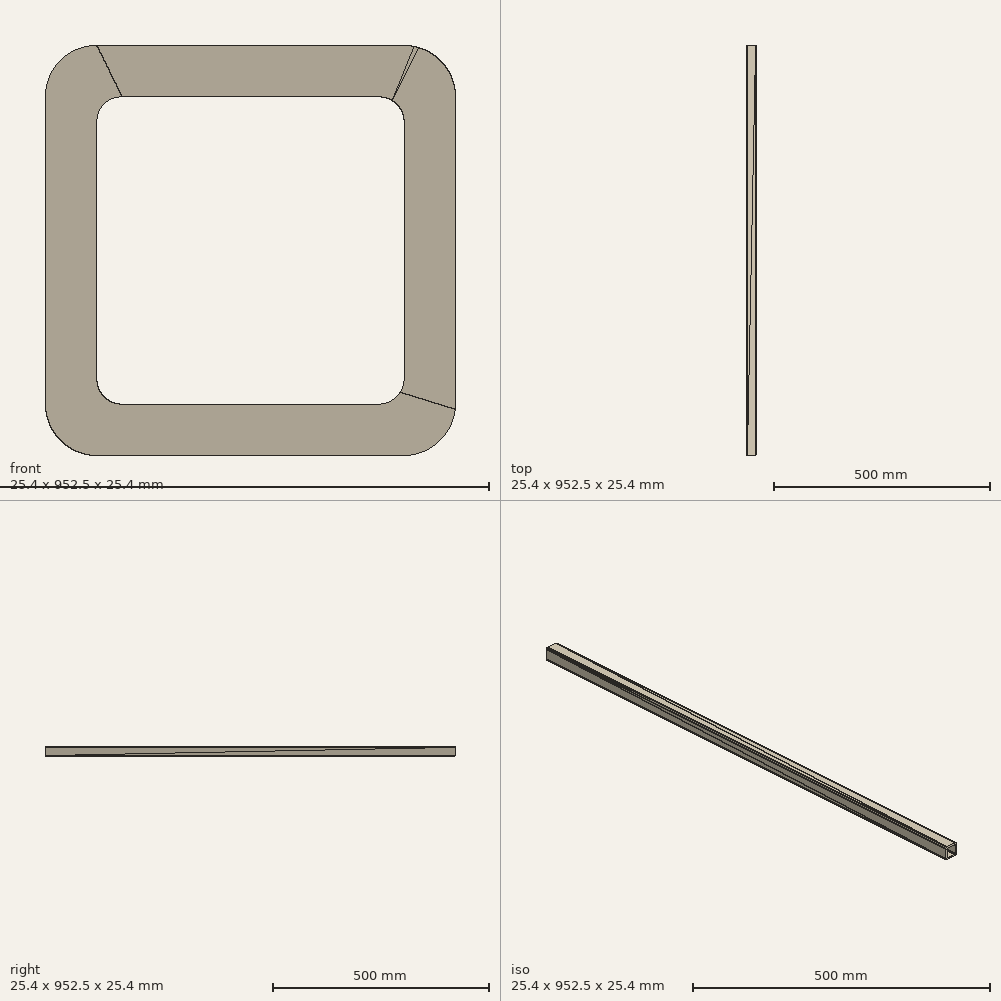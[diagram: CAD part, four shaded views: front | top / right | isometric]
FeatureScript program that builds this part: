
annotation { "Feature Type Name" : "Feature", "Feature Type Description" : "" }
export const myFeature = defineFeature(function(context is Context, id is Id, definition is map)
    precondition{}
    {
        {
            var Q0;
            Q0=qCreatedBy(makeId("Front.planeOp"),FACE);
            var sketch = newSketch(context, id + "F0", { "sketchPlane" : qUnion([Q0])});
            skLineSegment(sketch, "E0.bottom", {"start": v(3.18, 0) * mm, "end": v(22.23, 0) * mm});
            skLineSegment(sketch, "E0.top", {"start": v(3.17, 25.4) * mm, "end": v(22.23, 25.4) * mm});
            skLineSegment(sketch, "E0.left", {"start": v(0, 3.18) * mm, "end": v(0, 22.22) * mm});
            skLineSegment(sketch, "E0.right", {"start": v(25.4, 3.18) * mm, "end": v(25.4, 22.22) * mm});
            skPoint(sketch, "E1.visualSharp", {"position": v(0, 25.4) * mm});
            skArc(sketch, "E1.filletArc", {"start": v(3.17, 25.4) * mm, "mid": v(0.93, 24.47) * mm, "end": v(0, 22.22) * mm});
            skPoint(sketch, "E2.visualSharp", {"position": v(25.4, 25.4) * mm});
            skArc(sketch, "E2.filletArc", {"start": v(25.4, 22.22) * mm, "mid": v(24.47, 24.47) * mm, "end": v(22.23, 25.4) * mm});
            skPoint(sketch, "E3.visualSharp", {"position": v(25.4, 0) * mm});
            skArc(sketch, "E3.filletArc", {"start": v(22.23, 0) * mm, "mid": v(24.47, 0.93) * mm, "end": v(25.4, 3.18) * mm});
            skPoint(sketch, "E4.visualSharp", {"position": v(0, 0) * mm});
            skArc(sketch, "E4.filletArc", {"start": v(0, 3.18) * mm, "mid": v(0.93, 0.93) * mm, "end": v(3.18, 0) * mm});
            skSolve(sketch);
        }
        {
            var Q0;
            Q0 = qSketchRegion(id + "F0", true);
            extrude(context, id + "F1", {"entities" : qUnion([Q0]), "depth" : 952.5 * mm, "offsetDistance" : 25.4 * mm});
        }
        {
            var Q0;
            Q0=qCreatedBy(makeId("Front.planeOp"),FACE);
            var sketch = newSketch(context, id + "F2", { "sketchPlane" : qUnion([Q0])});
            skLineSegment(sketch, "E5.bottom", {"start": v(4.76, 3.18) * mm, "end": v(20.64, 3.18) * mm});
            skLineSegment(sketch, "E5.top", {"start": v(4.76, 22.23) * mm, "end": v(20.64, 22.23) * mm});
            skLineSegment(sketch, "E5.left", {"start": v(3.17, 4.76) * mm, "end": v(3.17, 20.64) * mm});
            skLineSegment(sketch, "E5.right", {"start": v(22.22, 4.76) * mm, "end": v(22.22, 20.64) * mm});
            skPoint(sketch, "E6.visualSharp", {"position": v(3.17, 22.23) * mm});
            skArc(sketch, "E6.filletArc", {"start": v(4.76, 22.23) * mm, "mid": v(3.64, 21.76) * mm, "end": v(3.17, 20.64) * mm});
            skPoint(sketch, "E7.visualSharp", {"position": v(22.22, 22.23) * mm});
            skArc(sketch, "E7.filletArc", {"start": v(22.22, 20.64) * mm, "mid": v(21.76, 21.76) * mm, "end": v(20.64, 22.23) * mm});
            skPoint(sketch, "E8.visualSharp", {"position": v(22.23, 3.18) * mm});
            skArc(sketch, "E8.filletArc", {"start": v(20.64, 3.18) * mm, "mid": v(21.76, 3.64) * mm, "end": v(22.22, 4.76) * mm});
            skPoint(sketch, "E9.visualSharp", {"position": v(3.18, 3.18) * mm});
            skArc(sketch, "E9.filletArc", {"start": v(3.18, 4.76) * mm, "mid": v(3.64, 3.64) * mm, "end": v(4.76, 3.18) * mm});
            skSolve(sketch);
        }
        {
            var Q0;
            Q0 = qSketchRegion(id + "F2", true);
            extrude(context, id + "F3", {"entities" : qUnion([Q0]), "operationType" : NewBodyOperationType.REMOVE, "depth" : 952.5 * mm, "offsetDistance" : 25.4 * mm});
        }
    });
